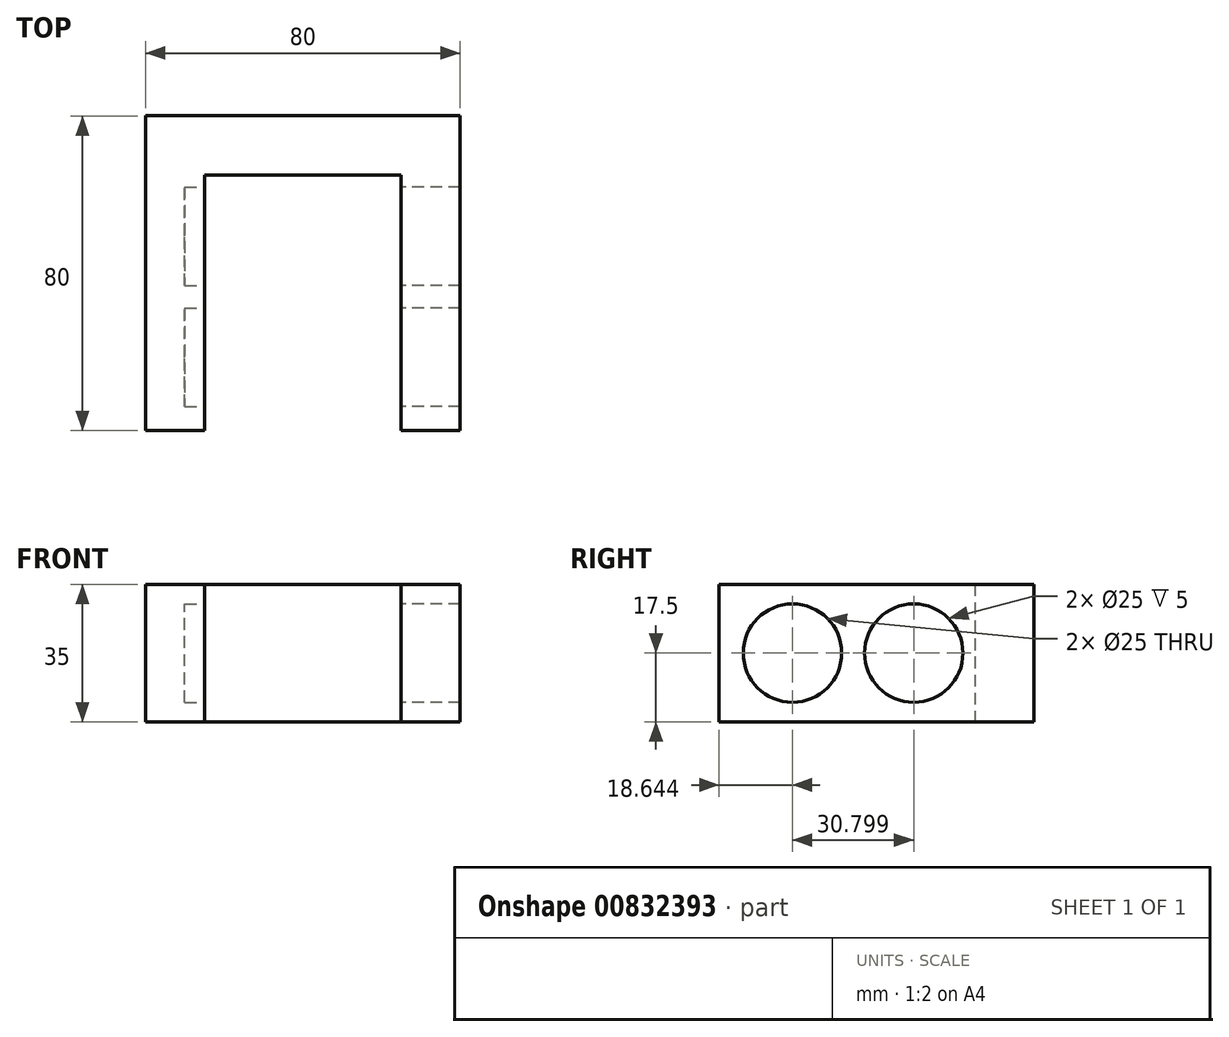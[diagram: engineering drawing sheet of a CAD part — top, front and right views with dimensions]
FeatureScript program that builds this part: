
annotation { "Feature Type Name" : "Feature", "Feature Type Description" : "" }
export const myFeature = defineFeature(function(context is Context, id is Id, definition is map)
    precondition{}
    {
        {
            var Q0;
            Q0=qCreatedBy(makeId("Top.planeOp"),FACE);
            var sketch = newSketch(context, id + "F0", { "sketchPlane" : qUnion([Q0])});
            skLineSegment(sketch, "E0.bottom", {"start": v(-52.9, 37.98) * mm, "end": v(-37.9, 37.98) * mm});
            skLineSegment(sketch, "E0.top", {"start": v(-52.9, -42.02) * mm, "end": v(-37.9, -42.02) * mm});
            skLineSegment(sketch, "E0.left", {"start": v(-52.9, 37.98) * mm, "end": v(-52.9, -42.02) * mm});
            skLineSegment(sketch, "E0.right", {"start": v(-37.9, 37.98) * mm, "end": v(-37.9, -42.02) * mm});
            skSolve(sketch);
        }
        {
            var Q0;
            Q0=makeQuery(id+"F0.imprint","IMPRINT",FACE,{"disambiguationData":[TD([[makeQuery(id+"F0.imprint","IMPRINT",EDGE,{"derivedFrom":sQuery(id+"F0.wireOp",EDGE,"E0.bottom")}),-1.0]])]});
            extrude(context, id + "F1", {"entities" : qUnion([Q0]), "depth" : 35 * mm, "offsetDistance" : 25 * mm});
        }
        {
            var Q0;
            Q0=makeQuery(id+"F1.opExtrude","SWEPT_FACE",FACE,{"disambiguationData":[OSD([sQuery(id+"F0.wireOp",EDGE,"E0.right")])]});
            var sketch = newSketch(context, id + "F2", { "sketchPlane" : qUnion([Q0])});
            skLineSegment(sketch, "E1.bottom", {"start": v(37.98, 35) * mm, "end": v(22.98, 35) * mm});
            skLineSegment(sketch, "E1.top", {"start": v(37.98, 0) * mm, "end": v(22.98, 0) * mm});
            skLineSegment(sketch, "E1.left", {"start": v(37.98, 35) * mm, "end": v(37.98, 0) * mm});
            skLineSegment(sketch, "E1.right", {"start": v(22.98, 35) * mm, "end": v(22.98, 0) * mm});
            skLineSegment(sketch, "E2", {"start": v(-42.02, 17.5) * mm, "end": v(22.98, 17.5) * mm, "construction": true});
            skCircle(sketch, "E3", {"center": v(-27.25, 17.5) * mm, "radius": 12.5 * mm});
            skCircle(sketch, "E4", {"center": v(6.5, 17.5) * mm, "radius": 12.5 * mm});
            skSolve(sketch);
        }
        {
            var Q0;
            Q0=makeQuery(id+"F2.imprint","IMPRINT",FACE,{"disambiguationData":[TD([[makeQuery(id+"F2.imprint","IMPRINT",EDGE,{"derivedFrom":sQuery(id+"F2.wireOp",EDGE,"E1.bottom")}),1.0]])]});
            extrude(context, id + "F3", {"entities" : qUnion([Q0]), "operationType" : NewBodyOperationType.ADD, "depth" : (80 - 15 - 15) * mm, "offsetDistance" : 25 * mm});
        }
        {
            var Q0;
            Q0=makeQuery(id+"F1.opExtrude","SWEPT_FACE",FACE,{"disambiguationData":[OSD([sQuery(id+"F0.wireOp",EDGE,"E0.right")])]});
            var sketch = newSketch(context, id + "F4", { "sketchPlane" : qUnion([Q0])});
            skLineSegment(sketch, "E5", {"start": v(-42.02, 17.5) * mm, "end": v(22.98, 17.5) * mm, "construction": true});
            skCircle(sketch, "E6", {"center": v(-23.38, 17.5) * mm, "radius": 12.5 * mm});
            skCircle(sketch, "E7", {"center": v(7.42, 17.5) * mm, "radius": 12.5 * mm});
            skSolve(sketch);
        }
        {
            var Q0;
            Q0=makeQuery(id+"F4.imprint","IMPRINT",FACE,{"disambiguationData":[TD([[makeQuery(id+"F4.imprint","IMPRINT",EDGE,{"derivedFrom":sQuery(id+"F4.wireOp",EDGE,"E6")}),1.0]])]});
            var Q1;
            Q1=makeQuery(id+"F4.imprint","IMPRINT",FACE,{"disambiguationData":[TD([[makeQuery(id+"F4.imprint","IMPRINT",EDGE,{"derivedFrom":sQuery(id+"F4.wireOp",EDGE,"E7")}),1.0]])]});
            extrude(context, id + "F5", {"entities" : qUnion([Q0, Q1]), "operationType" : NewBodyOperationType.REMOVE, "oppositeDirection" : true, "depth" : 5 * mm, "offsetDistance" : 25 * mm});
        }
        {
            var Q0;
            Q0=makeQuery(id+"F3.opExtrude","CAP_FACE",FACE,{"disambiguationData":[OSD([sQuery(id+"F2.wireOp",EDGE,"E1.bottom"),sQuery(id+"F2.wireOp",EDGE,"E1.top"),sQuery(id+"F2.wireOp",EDGE,"E1.left"),sQuery(id+"F2.wireOp",EDGE,"E1.right")])],"isStart":false});
            var sketch = newSketch(context, id + "F6", { "sketchPlane" : qUnion([Q0])});
            skLineSegment(sketch, "E8.bottom", {"start": v(37.98, 35) * mm, "end": v(-42.02, 35) * mm});
            skLineSegment(sketch, "E8.top", {"start": v(37.98, 0) * mm, "end": v(-42.02, 0) * mm});
            skLineSegment(sketch, "E8.left", {"start": v(37.98, 35) * mm, "end": v(37.98, 0) * mm});
            skLineSegment(sketch, "E8.right", {"start": v(-42.02, 35) * mm, "end": v(-42.02, 0) * mm});
            skSolve(sketch);
        }
        {
            var Q0;
            {var subQ0=sQuery(id+"F6.wireOp",EDGE,"E8.left");Q0=makeQuery(id+"F6.imprint","IMPRINT",FACE,{"disambiguationData":[TD([[makeQuery(id+"F6.imprint","IMPRINT",EDGE,{"derivedFrom":subQ0}),-1.0]])]});}
            var Q1;
            {var subQ2=sQuery(id+"F6.wireOp",EDGE,"E8.right");Q1=makeQuery(id+"F6.imprint","IMPRINT",FACE,{"disambiguationData":[TD([[makeQuery(id+"F6.imprint","IMPRINT",EDGE,{"derivedFrom":subQ2}),1.0]])]});}
            extrude(context, id + "F7", {"entities" : qUnion([Q0, Q1]), "operationType" : NewBodyOperationType.ADD, "depth" : 15 * mm, "offsetDistance" : 25 * mm});
        }
        {
            var Q0;
            Q0=makeQuery(id+"F5.boolean.opBoolean","COPY",FACE,{"derivedFrom":makeQuery(id+"F5.opExtrude","CAP_FACE",FACE,{"disambiguationData":[OSD([sQuery(id+"F4.wireOp",EDGE,"E6")])],"isStart":false})});
            var Q1;
            Q1=makeQuery(id+"F5.boolean.opBoolean","COPY",FACE,{"derivedFrom":makeQuery(id+"F5.opExtrude","CAP_FACE",FACE,{"disambiguationData":[OSD([sQuery(id+"F4.wireOp",EDGE,"E7")])],"isStart":false})});
            extrude(context, id + "F8", {"entities" : qUnion([Q0, Q1]), "operationType" : NewBodyOperationType.REMOVE, "depth" : 100 * mm, "offsetDistance" : 25 * mm});
        }
    });
